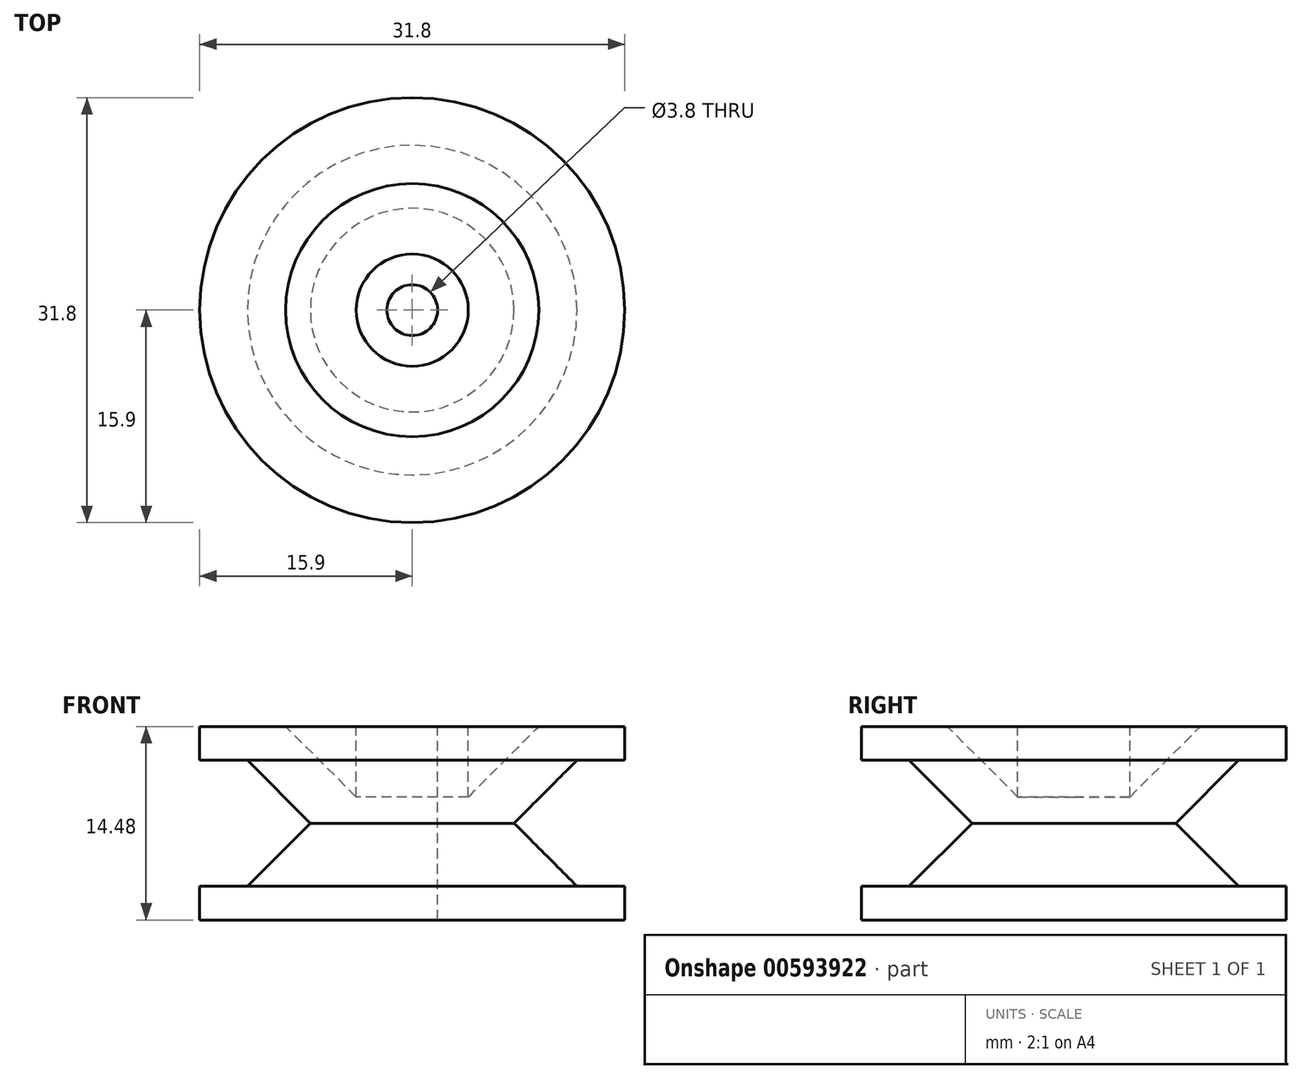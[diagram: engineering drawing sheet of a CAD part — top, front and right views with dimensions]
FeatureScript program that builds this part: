
annotation { "Feature Type Name" : "Feature", "Feature Type Description" : "" }
export const myFeature = defineFeature(function(context is Context, id is Id, definition is map)
    precondition{}
    {
        {
            var Q0;
            Q0=qCreatedBy(makeId("Top.planeOp"),FACE);
            var sketch = newSketch(context, id + "F0", { "sketchPlane" : qUnion([Q0])});
            skCircle(sketch, "E0", {"center": v(0, 0) * mm, "radius": 15.9 * mm});
            skSolve(sketch);
        }
        {
            var Q0;
            Q0=qSketchRegion(id+"F0",true);
            extrude(context, id + "F1", {"entities" : qUnion([Q0]), "endBound" : BoundingType.SYMMETRIC, "depth" : 14.48 * mm, "offsetDistance" : 25.4 * mm});
        }
        {
            var Q0;
            Q0=makeQuery(id+"F1.opExtrude","CAP_FACE",FACE,{"disambiguationData":[OSD([sQuery(id+"F0.wireOp",EDGE,"E0")])],"isStart":false});
            var sketch = newSketch(context, id + "F2", { "sketchPlane" : qUnion([Q0])});
            skCircle(sketch, "E1", {"center": v(0, 0) * mm, "radius": 1.9 * mm});
            skSolve(sketch);
        }
        {
            var Q0;
            Q0=makeQuery(id+"F2.imprint","IMPRINT",FACE,{"disambiguationData":[TD([[makeQuery(id+"F2.imprint","IMPRINT",EDGE,{"derivedFrom":sQuery(id+"F2.wireOp",EDGE,"E1")}),1.0]])]});
            extrude(context, id + "F3", {"entities" : qUnion([Q0]), "operationType" : NewBodyOperationType.REMOVE, "endBound" : BoundingType.THROUGH_ALL, "oppositeDirection" : true, "depth" : 25.4 * mm, "offsetDistance" : 25.4 * mm});
        }
        {
            var Q0;
            Q0=qCreatedBy(makeId("Right.planeOp"),FACE);
            var sketch = newSketch(context, id + "F4", { "sketchPlane" : qUnion([Q0])});
            skLineSegment(sketch, "E2", {"start": v(20.4, 4.71) * mm, "end": v(12.33, 4.71) * mm});
            skLineSegment(sketch, "E3", {"start": v(12.33, 4.71) * mm, "end": v(7.62, 0) * mm});
            skLineSegment(sketch, "E4", {"start": v(7.62, 0) * mm, "end": v(12.33, -4.71) * mm});
            skLineSegment(sketch, "E5", {"start": v(12.33, -4.71) * mm, "end": v(20.4, -4.71) * mm});
            skLineSegment(sketch, "E6", {"start": v(20.4, -4.71) * mm, "end": v(20.4, 4.71) * mm});
            skLineSegment(sketch, "E7", {"start": v(0, 0) * mm, "end": v(0, 9.8) * mm, "construction": true});
            skLineSegment(sketch, "E8", {"start": v(4.2, 9.06) * mm, "end": v(4.2, 1.96) * mm});
            skLineSegment(sketch, "E9", {"start": v(4.2, 1.96) * mm, "end": v(11.3, 9.06) * mm});
            skLineSegment(sketch, "E10", {"start": v(11.3, 9.06) * mm, "end": v(4.2, 9.06) * mm});
            skSolve(sketch);
        }
        {
            var Q0;
            Q0=qSketchRegion(id+"F4",true);
            var Q1;
            Q1=sQuery(id+"F4.wireOp",EDGE,"E7");
            revolve(context, id + "F5", {"operationType" : NewBodyOperationType.REMOVE, "entities" : qUnion([Q0]), "axis" : qUnion([Q1]), "revolveType" : RevolveType.FULL, "oppositeDirection" : true});
        }
    });
